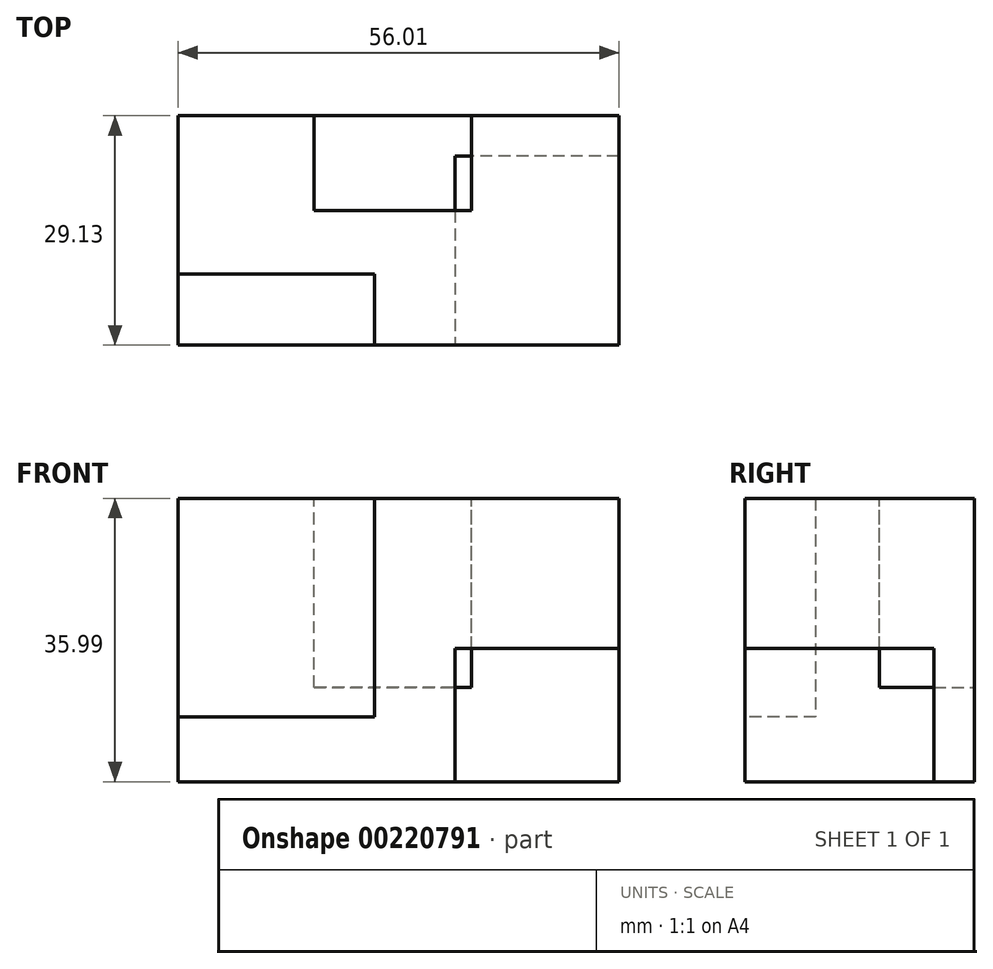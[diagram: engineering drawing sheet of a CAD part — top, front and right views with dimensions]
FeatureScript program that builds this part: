
annotation { "Feature Type Name" : "Feature", "Feature Type Description" : "" }
export const myFeature = defineFeature(function(context is Context, id is Id, definition is map)
    precondition{}
    {
        {
            var Q0;
            Q0=qCreatedBy(makeId("Top.planeOp"),FACE);
            var sketch = newSketch(context, id + "F0", { "sketchPlane" : qUnion([Q0])});
            skLineSegment(sketch, "E0.bottom", {"start": v(0, 0) * mm, "end": v(-56, 0) * mm});
            skLineSegment(sketch, "E0.top", {"start": v(0, 29.13) * mm, "end": v(-56, 29.13) * mm});
            skLineSegment(sketch, "E0.left", {"start": v(0, 0) * mm, "end": v(0, 29.13) * mm});
            skLineSegment(sketch, "E0.right", {"start": v(-56, 0) * mm, "end": v(-56, 29.13) * mm});
            skSolve(sketch);
        }
        {
            var Q0;
            Q0=makeQuery(id+"F0.imprint","IMPRINT",FACE,{"disambiguationData":[TD([[makeQuery(id+"F0.imprint","IMPRINT",EDGE,{"derivedFrom":sQuery(id+"F0.wireOp",EDGE,"E0.bottom")}),-1.0]])]});
            var sketch = newSketch(context, id + "F1", { "sketchPlane" : qUnion([Q0])});
            skSolve(sketch);
        }
        {
            var Q0;
            Q0 = qSketchRegion(id + "F1", true);
            var Q1;
            Q1=makeQuery(id+"F0.imprint","IMPRINT",FACE,{"disambiguationData":[TD([[makeQuery(id+"F0.imprint","IMPRINT",EDGE,{"derivedFrom":sQuery(id+"F0.wireOp",EDGE,"E0.bottom")}),-1.0]])]});
            extrude(context, id + "F2", {"entities" : qUnion([Q0, Q1]), "depth" : 36 * mm});
        }
        {
            var Q0;
            Q0=makeQuery(id+"F2.opExtrude","CAP_FACE",FACE,{"disambiguationData":[OSD([sQuery(id+"F0.wireOp",EDGE,"E0.bottom"),sQuery(id+"F0.wireOp",EDGE,"E0.top"),sQuery(id+"F0.wireOp",EDGE,"E0.left"),sQuery(id+"F0.wireOp",EDGE,"E0.right")])],"isStart":false});
            var sketch = newSketch(context, id + "F3", { "sketchPlane" : qUnion([Q0])});
            skLineSegment(sketch, "E1", {"start": v(-38.75, 29.13) * mm, "end": v(-38.75, 17.09) * mm});
            skLineSegment(sketch, "E2", {"start": v(-38.75, 17.09) * mm, "end": v(-18.76, 17.09) * mm});
            skLineSegment(sketch, "E3", {"start": v(-18.76, 17.09) * mm, "end": v(-18.76, 29.13) * mm});
            skSolve(sketch);
        }
        {
            var Q0;
            Q0 = qSketchRegion(id + "F3", true);
            var Q1;
            {var subQ0=sQuery(id+"F3.wireOp",EDGE,"E1");Q1=makeQuery(id+"F3.imprint","IMPRINT",FACE,{"disambiguationData":[TD([[makeQuery(id+"F3.imprint","IMPRINT",EDGE,{"derivedFrom":subQ0}),1.0]])]});}
            extrude(context, id + "F4", {"entities" : qUnion([Q0, Q1]), "operationType" : NewBodyOperationType.REMOVE, "oppositeDirection" : true, "depth" : 24 * mm});
        }
        {
            var Q0;
            Q0=makeQuery(id+"F2.opExtrude","SWEPT_FACE",FACE,{"disambiguationData":[OSD([sQuery(id+"F0.wireOp",EDGE,"E0.bottom")])]});
            var sketch = newSketch(context, id + "F5", { "sketchPlane" : qUnion([Q0])});
            skLineSegment(sketch, "E4.bottom", {"start": v(0, 0) * mm, "end": v(-20.85, 0) * mm});
            skLineSegment(sketch, "E4.top", {"start": v(0, 16.94) * mm, "end": v(-20.85, 16.94) * mm});
            skLineSegment(sketch, "E4.left", {"start": v(0, 0) * mm, "end": v(0, 16.94) * mm});
            skLineSegment(sketch, "E4.right", {"start": v(-20.85, 0) * mm, "end": v(-20.85, 16.94) * mm});
            skLineSegment(sketch, "E5", {"start": v(0, 16.94) * mm, "end": v(17, 33.88) * mm});
            skLineSegment(sketch, "E6", {"start": v(17, 33.88) * mm, "end": v(17, 16.94) * mm});
            skLineSegment(sketch, "E7.bottom", {"start": v(-56, 36) * mm, "end": v(-31.04, 36) * mm});
            skLineSegment(sketch, "E7.right", {"start": v(-31.04, 36) * mm, "end": v(-31.04, 24) * mm});
            skLineSegment(sketch, "E8", {"start": v(-31.04, 36) * mm, "end": v(-23.84, 41.38) * mm});
            skLineSegment(sketch, "E9", {"start": v(-23.84, 41.38) * mm, "end": v(-48.81, 41.38) * mm});
            skLineSegment(sketch, "E10", {"start": v(-56, 36) * mm, "end": v(-48.81, 41.38) * mm});
            skLineSegment(sketch, "E11", {"start": v(-19.05, 24) * mm, "end": v(-31.04, 24) * mm});
            skLineSegment(sketch, "E12", {"start": v(-31.04, 24) * mm, "end": v(-31.04, 8.26) * mm});
            skLineSegment(sketch, "E13", {"start": v(-31.04, 8.26) * mm, "end": v(-56, 8.26) * mm});
            skPoint(sketch, "E7.left.end.orphan", {"position": v(-56, 24) * mm});
            skSolve(sketch);
        }
        {
            var Q0;
            Q0=makeQuery(id+"F5.imprint","IMPRINT",FACE,{"disambiguationData":[TD([[makeQuery(id+"F5.imprint","IMPRINT",EDGE,{"derivedFrom":sQuery(id+"F5.wireOp",EDGE,"E4.bottom")}),-1.0]])]});
            var sketch = newSketch(context, id + "F6", { "sketchPlane" : qUnion([Q0])});
            skSolve(sketch);
        }
        {
            var Q0;
            Q0 = qSketchRegion(id + "F6", true);
            var Q1;
            Q1=makeQuery(id+"F5.imprint","IMPRINT",FACE,{"disambiguationData":[TD([[makeQuery(id+"F5.imprint","IMPRINT",EDGE,{"derivedFrom":sQuery(id+"F5.wireOp",EDGE,"E4.bottom")}),-1.0]])]});
            extrude(context, id + "F7", {"entities" : qUnion([Q0, Q1]), "operationType" : NewBodyOperationType.REMOVE, "oppositeDirection" : true, "depth" : 24 * mm});
        }
        {
            var Q0;
            Q0=makeQuery(id+"F5.imprint","IMPRINT",FACE,{"disambiguationData":[TD([[makeQuery(id+"F5.imprint","IMPRINT",EDGE,{"derivedFrom":sQuery(id+"F5.wireOp",EDGE,"E7.bottom")}),1.0]])]});
            extrude(context, id + "F8", {"entities" : qUnion([Q0]), "operationType" : NewBodyOperationType.REMOVE, "oppositeDirection" : true, "depth" : 9 * mm});
        }
    });
